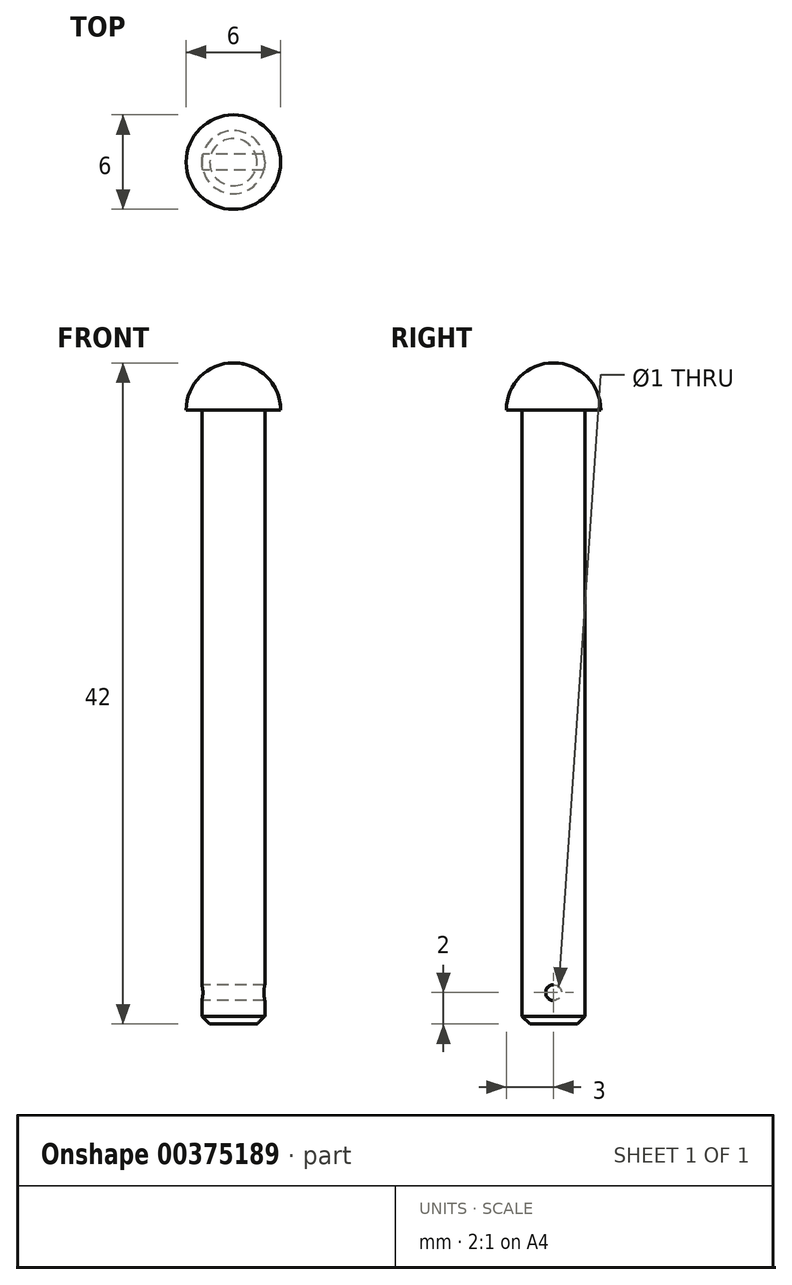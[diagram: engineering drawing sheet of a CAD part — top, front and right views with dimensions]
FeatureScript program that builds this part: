
annotation { "Feature Type Name" : "Feature", "Feature Type Description" : "" }
export const myFeature = defineFeature(function(context is Context, id is Id, definition is map)
    precondition{}
    {
        {
            var Q0;
            Q0=qCreatedBy(makeId("Top.planeOp"),FACE);
            var sketch = newSketch(context, id + "F0", { "sketchPlane" : qUnion([Q0])});
            skCircle(sketch, "E0", {"center": v(0, 0) * mm, "radius": 2 * mm});
            skSolve(sketch);
        }
        {
            var Q0;
            Q0=makeQuery(id+"F0.imprint","IMPRINT",FACE,{"disambiguationData":[TD([[makeQuery(id+"F0.imprint","IMPRINT",EDGE,{"derivedFrom":sQuery(id+"F0.wireOp",EDGE,"E0")}),1.0]])]});
            extrude(context, id + "F1", {"entities" : qUnion([Q0]), "depth" : 39 * mm});
        }
        {
            var Q0;
            Q0=makeQuery(id+"F1.opExtrude","CAP_EDGE",EDGE,{"disambiguationData":[OSD([sQuery(id+"F0.wireOp",EDGE,"E0")])],"isStart":true});
            chamfer(context, id + "F2", {"entities" : qUnion([Q0]), "chamferType" : ChamferType.OFFSET_ANGLE, "width" : .5 * mm, "oppositeDirection" : false, "angle" : 45 * degree, "tangentPropagation" : true});
        }
        {
            var Q0;
            Q0=makeQuery(id+"F1.opExtrude","CAP_FACE",FACE,{"disambiguationData":[OSD([sQuery(id+"F0.wireOp",EDGE,"E0")])],"isStart":false});
            var sketch = newSketch(context, id + "F3", { "sketchPlane" : qUnion([Q0])});
            skCircle(sketch, "E1", {"center": v(0, 0) * mm, "radius": 3 * mm});
            skSolve(sketch);
        }
        {
            var Q0;
            Q0 = qSketchRegion(id + "F3", true);
            extrude(context, id + "F4", {"entities" : qUnion([Q0]), "operationType" : NewBodyOperationType.ADD, "depth" : 3 * mm});
        }
        {
            var Q0;
            Q0=makeQuery(id+"F4.opExtrude","CAP_EDGE",EDGE,{"disambiguationData":[OSD([sQuery(id+"F3.wireOp",EDGE,"E1")])],"isStart":false});
            fillet(context, id + "F5", {"entities" : qUnion([Q0]), "radius" : 3 * mm, "tangentPropagation" : true, "allowEdgeOverflow" : false});
        }
        {
            var Q0;
            Q0=qCreatedBy(makeId("Right.planeOp"),FACE);
            var sketch = newSketch(context, id + "F6", { "sketchPlane" : qUnion([Q0])});
            skCircle(sketch, "E2", {"center": v(0, 2) * mm, "radius": 0.5 * mm});
            skSolve(sketch);
        }
        {
            var Q0;
            Q0 = qSketchRegion(id + "F6", true);
            extrude(context, id + "F7", {"entities" : qUnion([Q0]), "operationType" : NewBodyOperationType.REMOVE, "depth" : 25 * mm, "symmetric" : true});
        }
    });
